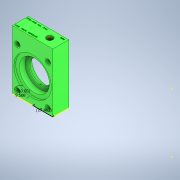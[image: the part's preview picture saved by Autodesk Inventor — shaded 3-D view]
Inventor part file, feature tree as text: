
AUTODESK INVENTOR PART (.ipt)
format: ipt  version: 2020 (Build 240168000, 168)  size: 539,648 bytes
history: native  units: in
note: dims shown in document units (in); Inventor stores cm internally (conversion verified against a paired STEP export)
features: sketch x4, hole x4, extrude x3, imported_body x1
ambient origin geometry x8: Origin, YZ Plane, XZ Plane, XY Plane, X Axis, Y Axis, Z Axis, Center Point
bodies: Solid1 (feature_tree)
feature tree (12):
  extrude  "Extrusion1"  Depth=0.3937in TaperAngle=0.0deg
  extrude  "Extrusion2"  Depth=0.3743in
  sketch  "Sketch3"  dims[d11=0.213in d12=0.2362in d13=0.4375in d14=0.25in d15=0.563in d16=0.375in d17=0.0in d18=0.3743in]
  hole  "Hole1"  [1 undecoded]
  hole  "Hole2"  [1 undecoded]
  hole  "Hole3"  [1 undecoded]
  hole  "Hole4"  [1 undecoded]
  extrude  "Extrusion3"  [1 undecoded]
  sketch  "Sketch1"  dims[d0=0.6398in d1=0.0in d2=0.3937in d3=0.0in]
  sketch  "Sketch2"  dims[d4=0.03in d5=0.2362in d6=0.4375in d7=0.25in d8=0.563in d9=0.9843in d10=0.8108in]
  sketch  "Sketch5"  dims[d19=0.0in d20=0.213in d21=0.2362in d22=0.4375in d23=0.25in d24=0.563in d25=0.25in d26=0.0in d27=0.03in d28=0.2362in d29=0.4375in d30=0.25in d31=0.563in d32=1.0in d33=0.8108in d34=0.1181in d35=0.0in d36=0.6875in]
  imported_body  "Base1"
note: 5 required parameter values undecoded (feature->parameter linkage not recoverable at this tier; creation-order binding heuristic only, values carry confidence <= 0.55)
